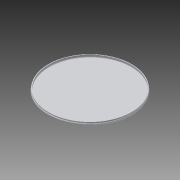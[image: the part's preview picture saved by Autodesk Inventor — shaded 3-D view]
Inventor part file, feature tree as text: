
AUTODESK INVENTOR PART (.ipt)
format: ipt  version: 2014 (Build 180170000, 170)  size: 113,664 bytes
history: native  units: in
note: dims shown in document units (in); Inventor stores cm internally (conversion verified against a paired STEP export)
features: revolve x1, sketch x1
ambient origin geometry x8: Origin, YZ Plane, XZ Plane, XY Plane, X Axis, Y Axis, Z Axis, Center Point
bodies: Solid1 (feature_tree)
feature tree (2):
  revolve  "Revolution1"  [1 undecoded]
  sketch  "Sketch1"  dims[d0=0.005in d1=0.0053in d2=90.0deg]
note: 1 required parameter value undecoded (feature->parameter linkage not recoverable at this tier; creation-order binding heuristic only, values carry confidence <= 0.55)
